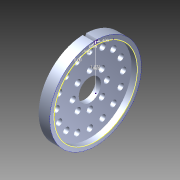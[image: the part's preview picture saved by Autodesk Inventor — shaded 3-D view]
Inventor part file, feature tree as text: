
AUTODESK INVENTOR PART (.ipt)
format: ipt  version: 2014 (Build 180170000, 170)  size: 339,968 bytes
history: native  units: in
note: dims shown in document units (in); Inventor stores cm internally (conversion verified against a paired STEP export)
features: other x2, sketch x1, imported_body x1
ambient origin geometry x8: Origin, YZ Plane, XZ Plane, XY Plane, X Axis, Y Axis, Z Axis, Center Point
bodies: Body1 (feature_tree)
feature tree (4):
  other  "9_64 (0.14063) Diameter Hole1"
  other  "User Library-6151941"
  sketch  "Sketch1"  dims[d0=25.1969in d2=0.0in d4=0.4in d5=0.9605in d6=0.4in d7=12.5984in d9=0.0in d11=1.0313in]
  imported_body  "Base1"
